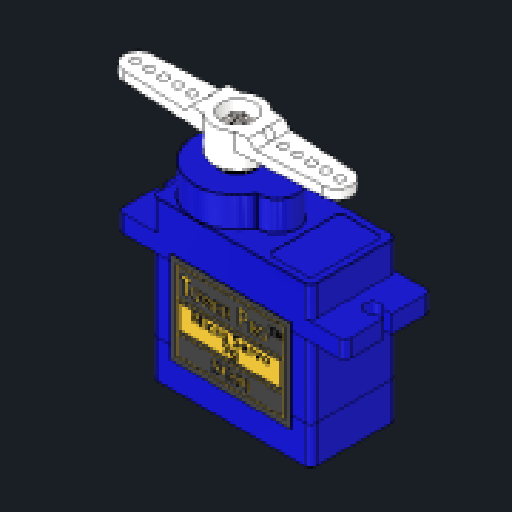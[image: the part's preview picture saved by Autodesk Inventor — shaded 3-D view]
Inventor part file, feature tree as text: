
AUTODESK INVENTOR PART (.ipt)
format: ipt  version: 2023.2 (Build 272271030, 271C)  size: 1,947,136 bytes
history: mixed  units: mm
features: other x18, extrude x1, chamfer x1, sketch x1, projected_geometry x1, imported_body x1
ambient origin geometry x8: Origin, YZ Plane, XZ Plane, XY Plane, X Axis, Y Axis, Z Axis, Center Point
bodies: Solid1 (imported_parasolid), Solid2 (imported_parasolid), Solid3 (imported_parasolid), Solid4 (imported_parasolid), Solid5 (imported_parasolid), Solid6 (imported_parasolid), Solid7 (imported_parasolid), Solid8 (imported_parasolid), Solid9 (imported_parasolid), Solid10 (imported_parasolid), Solid11 (imported_parasolid), Solid12 (imported_parasolid), Solid13 (imported_parasolid), Solid14 (imported_parasolid), Solid17 (imported_parasolid)
feature tree (23):
  other  "Plane4"
  other  "Plane4:1"
  other  "Plane4:2"
  extrude  "Extrusion1"  Depth=1.0mm TaperAngle=0.0deg
  chamfer  "Chamfer1"  Distance=1.0mm Angle=45.0deg
  sketch  "Sketch2"  dims[d7=10.0mm d8=1.0mm d9=0.0mm d10=1.0mm d11=2.0mm d12=45.0deg]
  projected_geometry  "Projected Loop1"
  other  "Tower Pro - Micro Servo 9g - SG90.1:1"
  other  "Tower Pro - Micro Servo 9g - SG90.1:2"
  other  "Tower Pro - Micro Servo 9g - SG90.1:3"
  other  "Tower Pro - Micro Servo 9g - SG90.1:4"
  other  "Tower Pro - Micro Servo 9g - SG90.1:5"
  other  "Tower Pro - Micro Servo 9g - SG90.1:6"
  other  "Tower Pro - Micro Servo 9g - SG90.1:7"
  other  "Tower Pro - Micro Servo 9g - SG90.1:8"
  other  "Tower Pro - Micro Servo 9g - SG90.1:9"
  other  "Tower Pro - Micro Servo 9g - SG90.1:10"
  other  "Tower Pro - Micro Servo 9g - SG90.1:11"
  other  "Tower Pro - Micro Servo 9g - SG90.1:12"
  other  "Tower Pro - Micro Servo 9g - SG90.1:13"
  other  "SG90 - Micro Servo 9g - Tower Pro.3:1"
  other  "SG90 - Micro Servo 9g - Tower Pro.6:1"
  imported_body  NMx_Import_Brep_tag  [imported B-rep: ~76 faces, bbox_mm=[18.75, 10.3, 12.4]]
